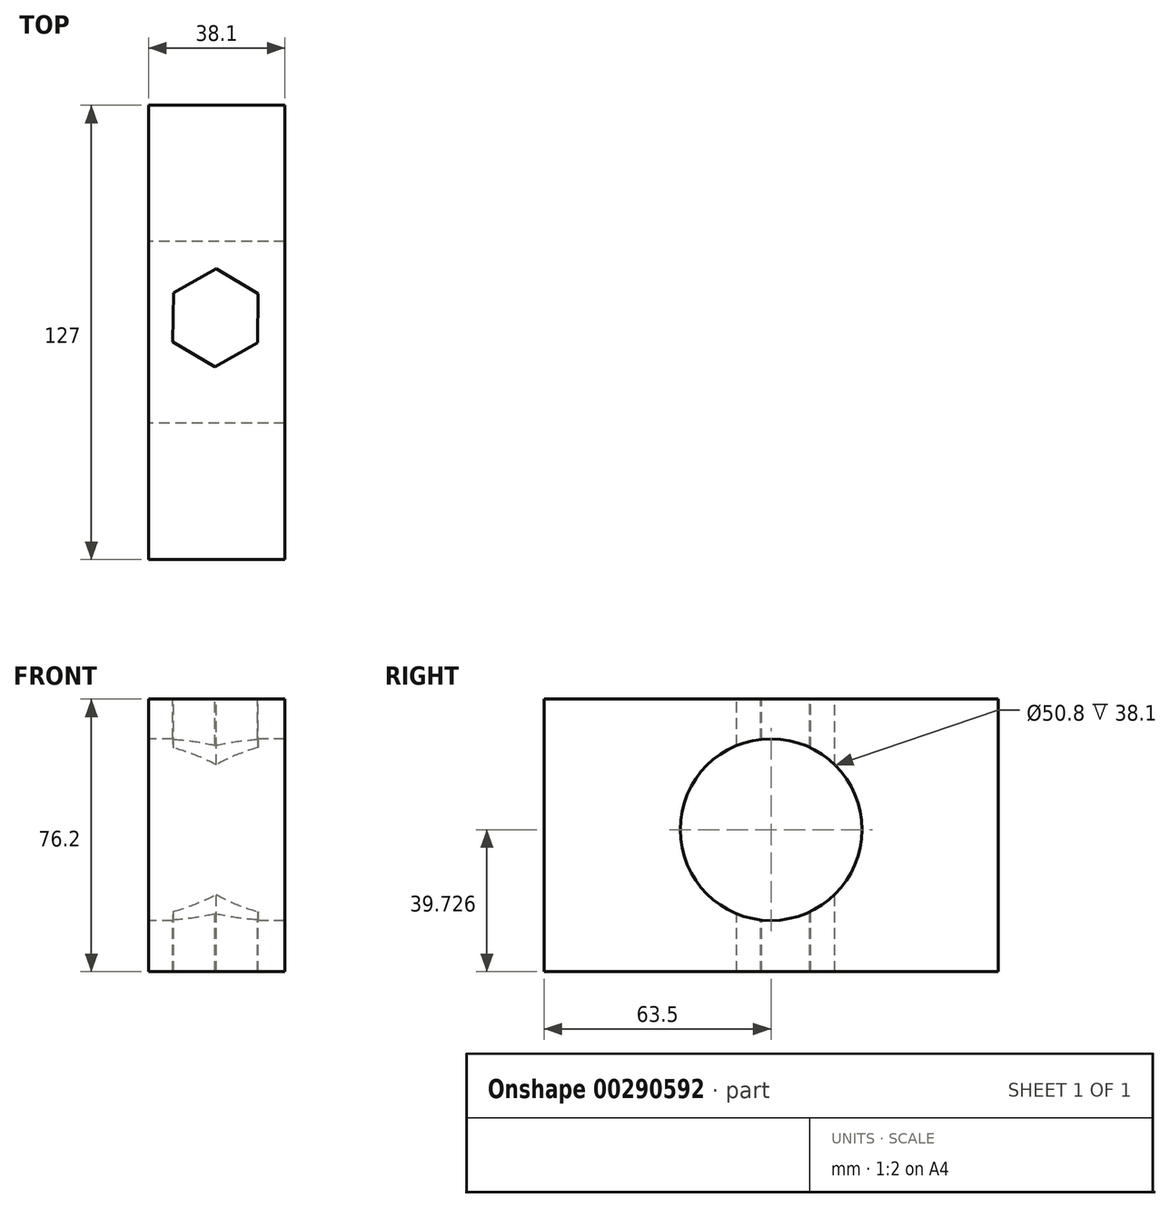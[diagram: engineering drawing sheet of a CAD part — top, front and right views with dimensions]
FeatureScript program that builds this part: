
annotation { "Feature Type Name" : "Feature", "Feature Type Description" : "" }
export const myFeature = defineFeature(function(context is Context, id is Id, definition is map)
    precondition{}
    {
        {
            var Q0;
            Q0=qCreatedBy(makeId("Front.planeOp"),FACE);
            var sketch = newSketch(context, id + "F0", { "sketchPlane" : qUnion([Q0])});
            skLineSegment(sketch, "E0.bottom", {"start": v(-71.73, 25.03) * mm, "end": v(-109.83, 25.03) * mm});
            skLineSegment(sketch, "E0.top", {"start": v(-71.73, -51.17) * mm, "end": v(-109.83, -51.17) * mm});
            skLineSegment(sketch, "E0.left", {"start": v(-71.73, 25.03) * mm, "end": v(-71.73, -51.17) * mm});
            skLineSegment(sketch, "E0.right", {"start": v(-109.83, 25.03) * mm, "end": v(-109.83, -51.17) * mm});
            skSolve(sketch);
        }
        {
            var Q0;
            Q0=makeQuery(id+"F0.imprint","IMPRINT",FACE,{"disambiguationData":[TD([[makeQuery(id+"F0.imprint","IMPRINT",EDGE,{"derivedFrom":sQuery(id+"F0.wireOp",EDGE,"E0.bottom")}),1.0]])]});
            extrude(context, id + "F1", {"entities" : qUnion([Q0]), "depth" : 127 * mm});
        }
        {
            var Q0;
            Q0=makeQuery(id+"F1.opExtrude","SWEPT_FACE",FACE,{"disambiguationData":[OSD([sQuery(id+"F0.wireOp",EDGE,"E0.right")])]});
            var sketch = newSketch(context, id + "F2", { "sketchPlane" : qUnion([Q0])});
            skCircle(sketch, "E1", {"center": v(63.5, -11.44) * mm, "radius": 25.4 * mm});
            skSolve(sketch);
        }
        {
            var Q0;
            Q0=makeQuery(id+"F2.imprint","IMPRINT",FACE,{"disambiguationData":[TD([[makeQuery(id+"F2.imprint","IMPRINT",EDGE,{"derivedFrom":sQuery(id+"F2.wireOp",EDGE,"E1")}),1.0]])]});
            extrude(context, id + "F3", {"entities" : qUnion([Q0]), "operationType" : NewBodyOperationType.REMOVE, "oppositeDirection" : true, "depth" : 101.6 * mm});
        }
        {
            var Q0;
            Q0=makeQuery(id+"F1.opExtrude","SWEPT_FACE",FACE,{"disambiguationData":[OSD([sQuery(id+"F0.wireOp",EDGE,"E0.bottom")])]});
            var sketch = newSketch(context, id + "F4", { "sketchPlane" : qUnion([Q0])});
            skCircle(sketch, "E2.cCircle", {"center": v(-91.1, -59.37) * mm, "radius": 11.86 * mm, "construction": true});
            skLineSegment(sketch, "E2.0", {"start": v(-102.89, -52.39) * mm, "end": v(-90.95, -45.67) * mm});
            skLineSegment(sketch, "E2.1", {"start": v(-90.95, -45.67) * mm, "end": v(-79.17, -52.65) * mm});
            skLineSegment(sketch, "E2.2", {"start": v(-79.17, -52.65) * mm, "end": v(-79.32, -66.35) * mm});
            skLineSegment(sketch, "E2.3", {"start": v(-79.32, -66.35) * mm, "end": v(-91.26, -73.06) * mm});
            skLineSegment(sketch, "E2.4", {"start": v(-91.26, -73.06) * mm, "end": v(-103.04, -66.08) * mm});
            skLineSegment(sketch, "E2.5", {"start": v(-103.04, -66.08) * mm, "end": v(-102.89, -52.39) * mm});
            skPoint(sketch, "E2.0.midPoint", {"position": v(-96.92, -49.03) * mm});
            skSolve(sketch);
        }
        {
            var Q0;
            Q0=makeQuery(id+"F4.imprint","IMPRINT",FACE,{"disambiguationData":[TD([[makeQuery(id+"F4.imprint","IMPRINT",EDGE,{"derivedFrom":sQuery(id+"F4.wireOp",EDGE,"E2.0")}),-1.0]])]});
            var Q1;
            Q1=makeQuery(id+"F1.opExtrude","SWEPT_FACE",FACE,{"disambiguationData":[OSD([sQuery(id+"F0.wireOp",EDGE,"E0.top")])]});
            extrude(context, id + "F5", {"entities" : qUnion([Q0]), "operationType" : NewBodyOperationType.REMOVE, "endBound" : BoundingType.UP_TO_SURFACE, "oppositeDirection" : true, "endBoundEntityFace" : qUnion([Q1]), "depth" : 25.4 * mm});
        }
    });
